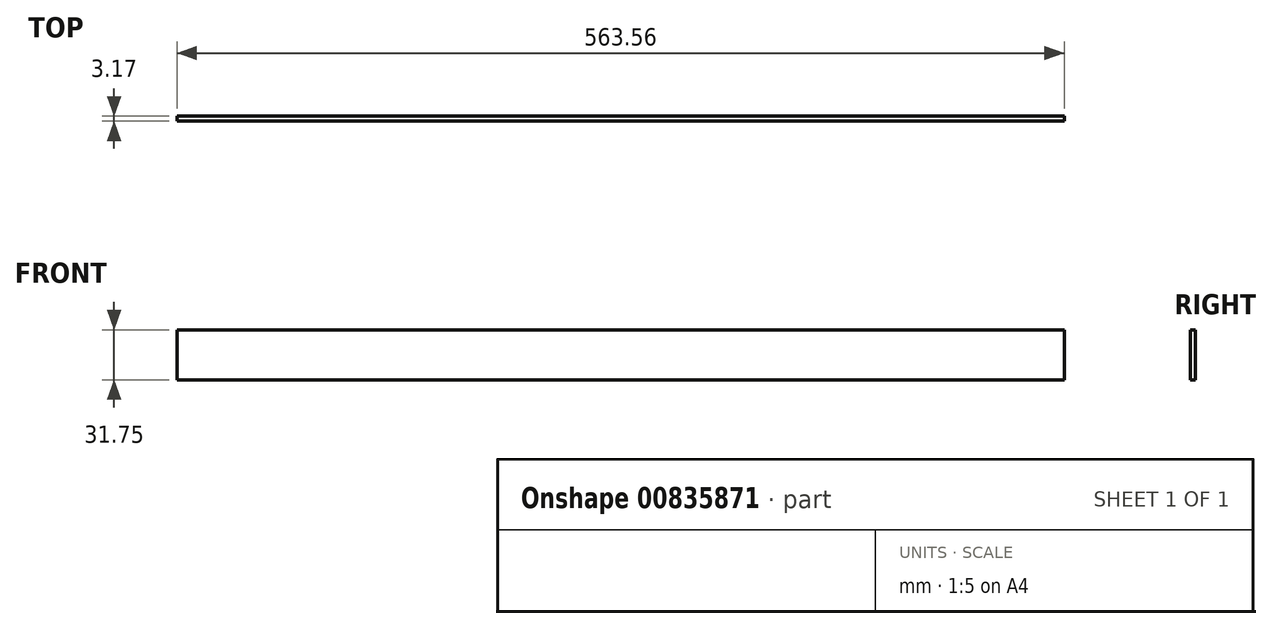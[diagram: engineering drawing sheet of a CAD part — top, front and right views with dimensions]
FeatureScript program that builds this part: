
annotation { "Feature Type Name" : "Feature", "Feature Type Description" : "" }
export const myFeature = defineFeature(function(context is Context, id is Id, definition is map)
    precondition{}
    {
        {
            var Q0;
            Q0=qCreatedBy(makeId("Right.planeOp"),FACE);
            var sketch = newSketch(context, id + "F0", { "sketchPlane" : qUnion([Q0])});
            skLineSegment(sketch, "E0.bottom", {"start": v(0, 0) * mm, "end": v(3.18, 0) * mm});
            skLineSegment(sketch, "E0.top", {"start": v(0, 31.75) * mm, "end": v(3.17, 31.75) * mm});
            skLineSegment(sketch, "E0.left", {"start": v(0, 0) * mm, "end": v(0, 31.75) * mm});
            skLineSegment(sketch, "E0.right", {"start": v(3.18, 0) * mm, "end": v(3.17, 31.75) * mm});
            skSolve(sketch);
        }
        {
            var Q0;
            Q0=qSketchRegion(id+"F0",true);
            extrude(context, id + "F1", {"entities" : qUnion([Q0]), "depth" : 563.56 * mm, "offsetDistance" : 25.4 * mm});
        }
    });
